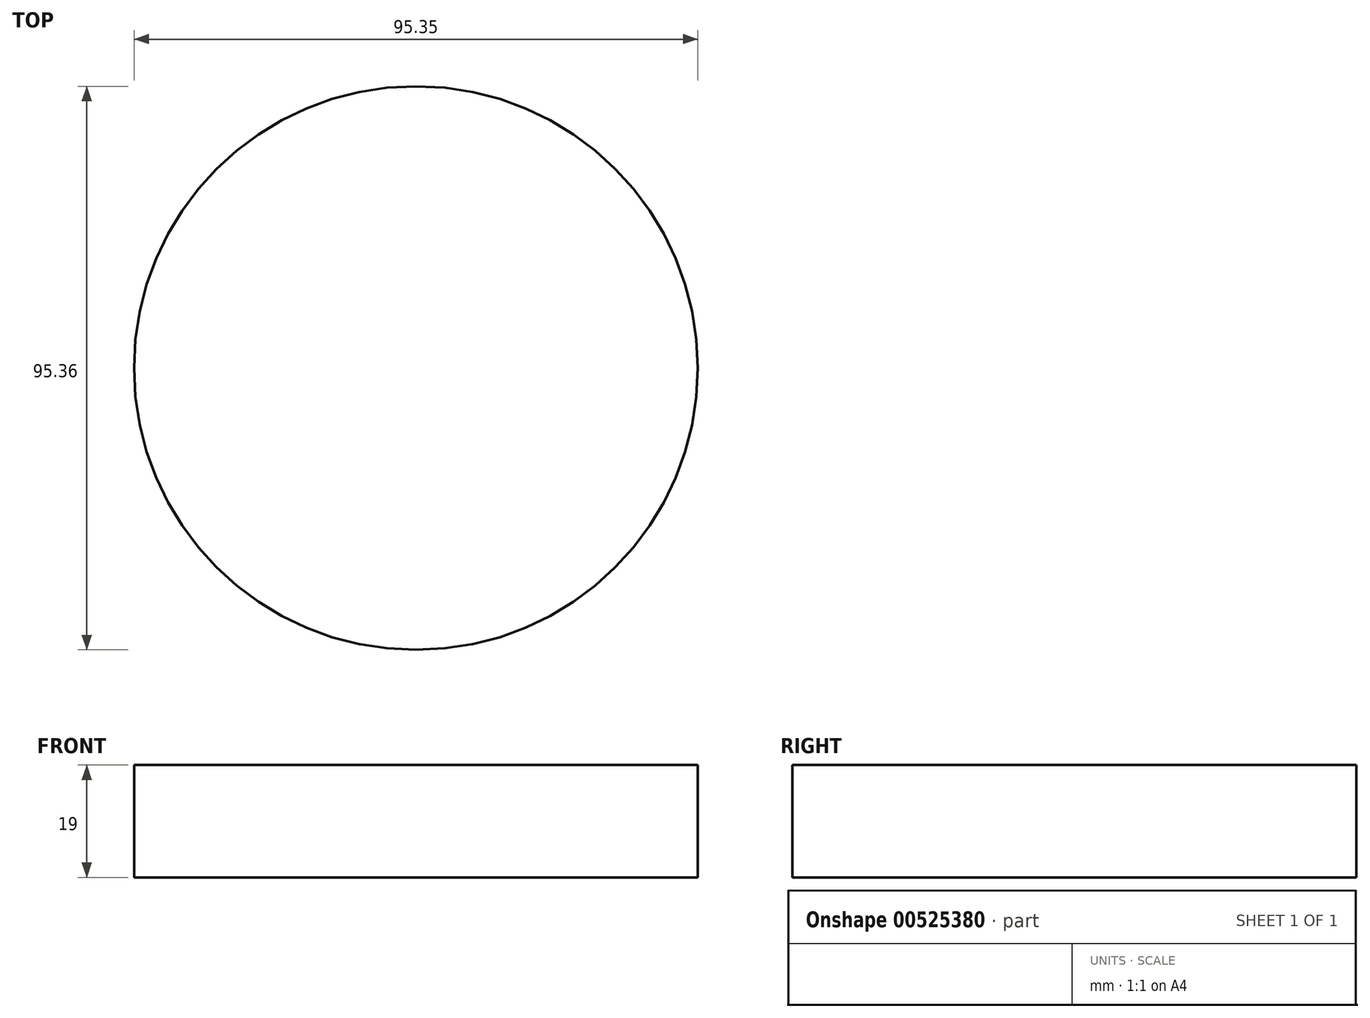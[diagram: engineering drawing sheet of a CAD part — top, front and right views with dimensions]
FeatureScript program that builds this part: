
annotation { "Feature Type Name" : "Feature", "Feature Type Description" : "" }
export const myFeature = defineFeature(function(context is Context, id is Id, definition is map)
    precondition{}
    {
        {
            var Q0;
            Q0=qCreatedBy(makeId("Top.planeOp"),FACE);
            var sketch = newSketch(context, id + "F0", { "sketchPlane" : qUnion([Q0])});
            skCircle(sketch, "E0", {"center": v(-24.3, 16.93) * mm, "radius": 47.68 * mm});
            skSolve(sketch);
        }
        {
            var Q0;
            Q0 = qSketchRegion(id + "F0", true);
            extrude(context, id + "F1", {"entities" : qUnion([Q0]), "depth" : 19 * mm, "offsetDistance" : 25 * mm});
        }
    });
